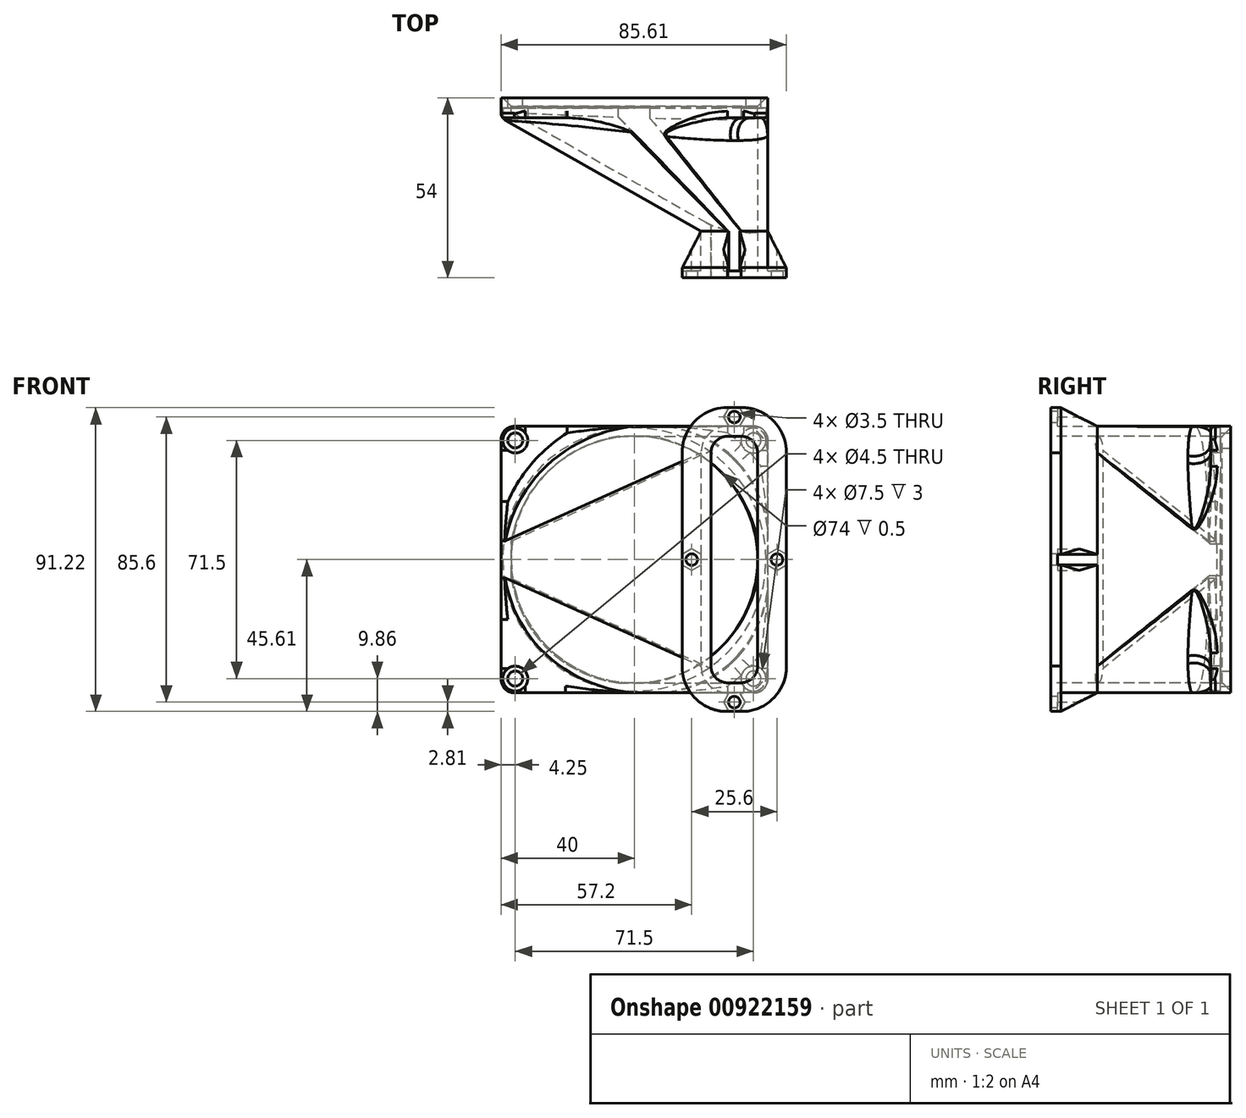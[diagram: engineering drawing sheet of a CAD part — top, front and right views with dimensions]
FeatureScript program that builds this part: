
annotation { "Feature Type Name" : "Feature", "Feature Type Description" : "" }
export const myFeature = defineFeature(function(context is Context, id is Id, definition is map)
    precondition{}
    {
        {
            var Q0;
            Q0=qCreatedBy(makeId("Front.planeOp"),FACE);
            var sketch = newSketch(context, id + "F0", { "sketchPlane" : qUnion([Q0])});
            skLineSegment(sketch, "E0.bottom", {"start": v(40, -40) * mm, "end": v(-40, -40) * mm});
            skLineSegment(sketch, "E0.top", {"start": v(40, 40) * mm, "end": v(-40, 40) * mm});
            skLineSegment(sketch, "E0.left", {"start": v(40, -40) * mm, "end": v(40, 40) * mm});
            skLineSegment(sketch, "E0.right", {"start": v(-40, -40) * mm, "end": v(-40, 40) * mm});
            skPoint(sketch, "E0.middle", {"position": v(0, 0) * mm});
            skCircle(sketch, "E1", {"center": v(0, 0) * mm, "radius": 37 * mm});
            skLineSegment(sketch, "E2.bottom", {"start": v(35.75, -35.75) * mm, "end": v(-35.75, -35.75) * mm, "construction": true});
            skLineSegment(sketch, "E2.top", {"start": v(35.75, 35.75) * mm, "end": v(-35.75, 35.75) * mm, "construction": true});
            skLineSegment(sketch, "E2.left", {"start": v(35.75, -35.75) * mm, "end": v(35.75, 35.75) * mm, "construction": true});
            skLineSegment(sketch, "E2.right", {"start": v(-35.75, -35.75) * mm, "end": v(-35.75, 35.75) * mm, "construction": true});
            skCircle(sketch, "E3", {"center": v(-35.75, 35.75) * mm, "radius": 2.25 * mm});
            skCircle(sketch, "E4", {"center": v(35.75, 35.75) * mm, "radius": 2.25 * mm});
            skCircle(sketch, "E5", {"center": v(-35.75, -35.75) * mm, "radius": 2.25 * mm});
            skCircle(sketch, "E6", {"center": v(35.75, -35.75) * mm, "radius": 2.25 * mm});
            skSolve(sketch);
        }
        {
            var Q0;
            Q0 = qSketchRegion(id + "F0", true);
            extrude(context, id + "F1", {"entities" : qUnion([Q0]), "depth" : 3 * mm, "offsetDistance" : 25 * mm});
        }
        {
            var Q0;
            Q0=makeQuery(id+"F1.opExtrude","CAP_FACE",FACE,{"disambiguationData":[OSD([sQuery(id+"F0.wireOp",EDGE,"E0.bottom"),sQuery(id+"F0.wireOp",EDGE,"E0.top"),sQuery(id+"F0.wireOp",EDGE,"E0.left"),sQuery(id+"F0.wireOp",EDGE,"E0.right"),sQuery(id+"F0.wireOp",EDGE,"E1"),sQuery(id+"F0.wireOp",EDGE,"E3"),sQuery(id+"F0.wireOp",EDGE,"E4"),sQuery(id+"F0.wireOp",EDGE,"E5"),sQuery(id+"F0.wireOp",EDGE,"E6")])],"isStart":false});
            var sketch = newSketch(context, id + "F2", { "sketchPlane" : qUnion([Q0])});
            skLineSegment(sketch, "E7", {"start": v(-5, 40) * mm, "end": v(0, 40) * mm});
            skLineSegment(sketch, "E8", {"start": v(40, -5) * mm, "end": v(40, 0) * mm});
            skLineSegment(sketch, "E9", {"start": v(0, -40) * mm, "end": v(-5, -40) * mm});
            skLineSegment(sketch, "E10", {"start": v(-40, 0) * mm, "end": v(-40, -5) * mm});
            skLineSegment(sketch, "E11", {"start": v(-40, 0) * mm, "end": v(-40, 5) * mm});
            skLineSegment(sketch, "E12", {"start": v(0, 40) * mm, "end": v(5, 40) * mm});
            skLineSegment(sketch, "E13", {"start": v(0, -40) * mm, "end": v(5, -40) * mm});
            skLineSegment(sketch, "E14", {"start": v(40, 0) * mm, "end": v(40, 5) * mm});
            skArc(sketch, "E15", {"start": v(-40, -5) * mm, "mid": v(-28.53, -28.53) * mm, "end": v(-5, -40) * mm});
            skArc(sketch, "E16", {"start": v(-5, 40) * mm, "mid": v(-28.28, 28.28) * mm, "end": v(-40, 5) * mm});
            skArc(sketch, "E17", {"start": v(40, 5) * mm, "mid": v(28.28, 28.28) * mm, "end": v(5, 40) * mm});
            skArc(sketch, "E18", {"start": v(5, -40) * mm, "mid": v(28.28, -28.28) * mm, "end": v(40, -5) * mm});
            skSolve(sketch);
        }
        {
            var Q0;
            Q0 = qSketchRegion(id + "F2", true);
            extrude(context, id + "F3", {"entities" : qUnion([Q0]), "operationType" : NewBodyOperationType.ADD, "depth" : 3 * mm, "offsetDistance" : 25 * mm});
        }
        {
            var Q0;
            Q0=makeQuery(id+"F1.opExtrude","CAP_FACE",FACE,{"disambiguationData":[OSD([sQuery(id+"F0.wireOp",EDGE,"E0.bottom"),sQuery(id+"F0.wireOp",EDGE,"E0.top"),sQuery(id+"F0.wireOp",EDGE,"E0.left"),sQuery(id+"F0.wireOp",EDGE,"E0.right"),sQuery(id+"F0.wireOp",EDGE,"E1"),sQuery(id+"F0.wireOp",EDGE,"E3"),sQuery(id+"F0.wireOp",EDGE,"E4"),sQuery(id+"F0.wireOp",EDGE,"E5"),sQuery(id+"F0.wireOp",EDGE,"E6")])],"isStart":true});
            cPlane(context, id + "F4", {"entities" : qUnion([Q0]), "cplaneType" : CPlaneType.OFFSET, "offset" : 40 * mm, "oppositeDirection" : true, "width" : 150 * mm, "height" : 150 * mm});
        }
        {
            var Q0;
            Q0=qCreatedBy(id+"F4.planeOp",FACE);
            var sketch = newSketch(context, id + "F5", { "sketchPlane" : qUnion([Q0])});
            skLineSegment(sketch, "E19.bottom", {"start": v(-28, 40) * mm, "end": v(-32, 40) * mm});
            skLineSegment(sketch, "E19.top", {"start": v(-28, -40) * mm, "end": v(-32, -40) * mm});
            skLineSegment(sketch, "E19.right", {"start": v(-40, 32) * mm, "end": v(-40, -32) * mm});
            skLineSegment(sketch, "E20", {"start": v(-20, 32) * mm, "end": v(-20, -32) * mm});
            skPoint(sketch, "E19.left.start.orphan", {"position": v(0, 40) * mm});
            skPoint(sketch, "E21.visualSharp", {"position": v(-40, -40) * mm});
            skArc(sketch, "E21.filletArc", {"start": v(-40, -32) * mm, "mid": v(-37.66, -37.66) * mm, "end": v(-32, -40) * mm});
            skPoint(sketch, "E22.visualSharp", {"position": v(-20, -40) * mm});
            skArc(sketch, "E22.filletArc", {"start": v(-28, -40) * mm, "mid": v(-22.34, -37.66) * mm, "end": v(-20, -32) * mm});
            skPoint(sketch, "E23.visualSharp", {"position": v(-20, 40) * mm});
            skArc(sketch, "E23.filletArc", {"start": v(-20, 32) * mm, "mid": v(-22.34, 37.66) * mm, "end": v(-28, 40) * mm});
            skPoint(sketch, "E24.visualSharp", {"position": v(-40, 40) * mm});
            skArc(sketch, "E24.filletArc", {"start": v(-32, 40) * mm, "mid": v(-37.66, 37.66) * mm, "end": v(-40, 32) * mm});
            skSolve(sketch);
        }
        {
            var Q1;
            Q1=makeQuery(id+"F3.opExtrude","CAP_FACE",FACE,{"disambiguationData":[OSD([sQuery(id+"F2.wireOp",EDGE,"E7"),sQuery(id+"F2.wireOp",EDGE,"E8"),sQuery(id+"F2.wireOp",EDGE,"E9"),sQuery(id+"F2.wireOp",EDGE,"E10"),sQuery(id+"F2.wireOp",EDGE,"E11"),sQuery(id+"F2.wireOp",EDGE,"E12"),sQuery(id+"F2.wireOp",EDGE,"E13"),sQuery(id+"F2.wireOp",EDGE,"E14"),sQuery(id+"F2.wireOp",EDGE,"E15"),sQuery(id+"F2.wireOp",EDGE,"E16"),sQuery(id+"F2.wireOp",EDGE,"E17"),sQuery(id+"F2.wireOp",EDGE,"E18")])],"isStart":false});
            var Q2;
            Q2=makeQuery(id+"F5.imprint","IMPRINT",FACE,{"disambiguationData":[TD([[makeQuery(id+"F5.imprint","IMPRINT",EDGE,{"derivedFrom":sQuery(id+"F5.wireOp",EDGE,"E19.bottom")}),1.0]])]});
            loft(context, id + "F6", {"operationType" : NewBodyOperationType.ADD, "sheetProfilesArray" : [{ "sheetProfileEntities" : qUnion([Q1]) }, { "sheetProfileEntities" : qUnion([Q2]) }]});
        }
        {
            var Q0;
            Q0=makeQuery(id+"F6.opLoft","CAP_FACE",FACE,{"disambiguationData":[OSD([makeQuery(id+"F5.imprint","IMPRINT",FACE,{"disambiguationData":[TD([[makeQuery(id+"F5.imprint","IMPRINT",EDGE,{"derivedFrom":sQuery(id+"F5.wireOp",EDGE,"E19.bottom")}),1.0]])]})])],"isStart":true});
            extrude(context, id + "F7", {"entities" : qUnion([Q0]), "operationType" : NewBodyOperationType.ADD, "depth" : 14 * mm, "offsetDistance" : 25 * mm});
        }
        {
            var Q0;
            Q0=makeQuery(id+"F7.opExtrude","CAP_FACE",FACE,{"disambiguationData":[OSD([makeQuery(id+"F5.imprint","IMPRINT",FACE,{"disambiguationData":[TD([[makeQuery(id+"F5.imprint","IMPRINT",EDGE,{"derivedFrom":sQuery(id+"F5.wireOp",EDGE,"E19.bottom")}),1.0]])]})])],"isStart":false});
            var Q1;
            Q1=makeQuery(id+"F3.opExtrude","CAP_FACE",FACE,{"disambiguationData":[OSD([sQuery(id+"F2.wireOp",EDGE,"E7"),sQuery(id+"F2.wireOp",EDGE,"E8"),sQuery(id+"F2.wireOp",EDGE,"E9"),sQuery(id+"F2.wireOp",EDGE,"E10"),sQuery(id+"F2.wireOp",EDGE,"E11"),sQuery(id+"F2.wireOp",EDGE,"E12"),sQuery(id+"F2.wireOp",EDGE,"E13"),sQuery(id+"F2.wireOp",EDGE,"E14"),sQuery(id+"F2.wireOp",EDGE,"E15"),sQuery(id+"F2.wireOp",EDGE,"E16"),sQuery(id+"F2.wireOp",EDGE,"E17"),sQuery(id+"F2.wireOp",EDGE,"E18")])],"isStart":true});
            shell(context, id + "F8", {"entities" : qUnion([Q0, Q1]), "thickness" : 3 * mm});
        }
        {
            var Q0;
            {var subQ0=sQuery(id+"F0.wireOp",EDGE,"E5");var subQ1=sQuery(id+"F0.wireOp",EDGE,"E0.right");var subQ2=sQuery(id+"F0.wireOp",EDGE,"E0.bottom");Q0=makeQuery(id+"F3.boolean.opBoolean","SPLIT",FACE,{"disambiguationData":[TD([makeQuery(id+"F1.opExtrude","SWEPT_FACE",FACE,{"disambiguationData":[OSD([subQ0])]})])],"derivedFrom":makeQuery(id+"F1.opExtrude","CAP_FACE",FACE,{"disambiguationData":[OSD([subQ2,sQuery(id+"F0.wireOp",EDGE,"E0.top"),sQuery(id+"F0.wireOp",EDGE,"E0.left"),subQ1,sQuery(id+"F0.wireOp",EDGE,"E1"),sQuery(id+"F0.wireOp",EDGE,"E3"),sQuery(id+"F0.wireOp",EDGE,"E4"),subQ0,sQuery(id+"F0.wireOp",EDGE,"E6")])],"isStart":false})});}
            var Q1;
            {var subQ0=sQuery(id+"F0.wireOp",EDGE,"E0.left");var subQ1=sQuery(id+"F0.wireOp",EDGE,"E6");var subQ2=sQuery(id+"F0.wireOp",EDGE,"E0.bottom");Q1=makeQuery(id+"F3.boolean.opBoolean","SPLIT",FACE,{"disambiguationData":[TD([makeQuery(id+"F1.opExtrude","SWEPT_FACE",FACE,{"disambiguationData":[OSD([subQ1])]})])],"derivedFrom":makeQuery(id+"F1.opExtrude","CAP_FACE",FACE,{"disambiguationData":[OSD([subQ2,sQuery(id+"F0.wireOp",EDGE,"E0.top"),subQ0,sQuery(id+"F0.wireOp",EDGE,"E0.right"),sQuery(id+"F0.wireOp",EDGE,"E1"),sQuery(id+"F0.wireOp",EDGE,"E3"),sQuery(id+"F0.wireOp",EDGE,"E4"),sQuery(id+"F0.wireOp",EDGE,"E5"),subQ1])],"isStart":false})});}
            var Q2;
            {var subQ0=sQuery(id+"F0.wireOp",EDGE,"E3");var subQ1=sQuery(id+"F0.wireOp",EDGE,"E0.right");var subQ2=sQuery(id+"F0.wireOp",EDGE,"E0.top");Q2=makeQuery(id+"F3.boolean.opBoolean","SPLIT",FACE,{"disambiguationData":[TD([makeQuery(id+"F1.opExtrude","SWEPT_FACE",FACE,{"disambiguationData":[OSD([subQ0])]})])],"derivedFrom":makeQuery(id+"F1.opExtrude","CAP_FACE",FACE,{"disambiguationData":[OSD([sQuery(id+"F0.wireOp",EDGE,"E0.bottom"),subQ2,sQuery(id+"F0.wireOp",EDGE,"E0.left"),subQ1,sQuery(id+"F0.wireOp",EDGE,"E1"),subQ0,sQuery(id+"F0.wireOp",EDGE,"E4"),sQuery(id+"F0.wireOp",EDGE,"E5"),sQuery(id+"F0.wireOp",EDGE,"E6")])],"isStart":false})});}
            var Q3;
            {var subQ0=sQuery(id+"F0.wireOp",EDGE,"E4");var subQ1=sQuery(id+"F0.wireOp",EDGE,"E0.left");var subQ2=sQuery(id+"F0.wireOp",EDGE,"E0.top");Q3=makeQuery(id+"F3.boolean.opBoolean","SPLIT",FACE,{"disambiguationData":[TD([makeQuery(id+"F1.opExtrude","SWEPT_FACE",FACE,{"disambiguationData":[OSD([subQ0])]})])],"derivedFrom":makeQuery(id+"F1.opExtrude","CAP_FACE",FACE,{"disambiguationData":[OSD([sQuery(id+"F0.wireOp",EDGE,"E0.bottom"),subQ2,subQ1,sQuery(id+"F0.wireOp",EDGE,"E0.right"),sQuery(id+"F0.wireOp",EDGE,"E1"),sQuery(id+"F0.wireOp",EDGE,"E3"),subQ0,sQuery(id+"F0.wireOp",EDGE,"E5"),sQuery(id+"F0.wireOp",EDGE,"E6")])],"isStart":false})});}
            var Q4;
            {var subQ0=sQuery(id+"F2.wireOp",EDGE,"E15");var subQ1=sQuery(id+"F2.wireOp",EDGE,"E9");var subQ2=sQuery(id+"F0.wireOp",EDGE,"E0.bottom");Q4=makeQuery(id+"F6.boolean.opBoolean","MERGE",VERTEX,{"derivedFrom":[makeQuery(id+"F3.opExtrude","CAP_VERTEX",VERTEX,{"disambiguationData":[OSD([subQ2,subQ1,subQ0])],"isStart":false}),makeQuery(id+"F6.opLoft","MID_CAP_VERTEX",VERTEX,{"disambiguationData":[OSD([subQ2,subQ1,subQ0])],"capPos":0.0})]});}
            extrude(context, id + "F9", {"entities" : qUnion([Q0, Q1, Q2, Q3]), "operationType" : NewBodyOperationType.ADD, "endBound" : BoundingType.UP_TO_VERTEX, "depth" : 25 * mm, "endBoundEntityVertex" : qUnion([Q4]), "offsetDistance" : 25 * mm});
        }
        {
            var Q0;
            {var subQ0=sQuery(id+"F0.wireOp",EDGE,"E5");var subQ1=sQuery(id+"F0.wireOp",EDGE,"E0.right");var subQ2=sQuery(id+"F0.wireOp",EDGE,"E0.bottom");var subQ3=sQuery(id+"F0.wireOp",EDGE,"E6");var subQ4=sQuery(id+"F0.wireOp",EDGE,"E4");var subQ5=sQuery(id+"F0.wireOp",EDGE,"E3");var subQ6=sQuery(id+"F0.wireOp",EDGE,"E1");var subQ7=sQuery(id+"F0.wireOp",EDGE,"E0.left");var subQ8=sQuery(id+"F0.wireOp",EDGE,"E0.top");Q0=makeQuery(id+"F9.opExtrude","CAP_FACE",FACE,{"disambiguationData":[OSD([subQ2,subQ8,subQ7,subQ1,subQ6,subQ5,subQ4,subQ0,subQ3]),TDD([makeQuery(id+"F3.boolean.opBoolean","SPLIT",FACE,{"disambiguationData":[TD([makeQuery(id+"F1.opExtrude","SWEPT_FACE",FACE,{"disambiguationData":[OSD([subQ0])]})])],"derivedFrom":makeQuery(id+"F1.opExtrude","CAP_FACE",FACE,{"disambiguationData":[OSD([subQ2,subQ8,subQ7,subQ1,subQ6,subQ5,subQ4,subQ0,subQ3])],"isStart":false})})])],"isStart":false});}
            var sketch = newSketch(context, id + "F10", { "sketchPlane" : qUnion([Q0])});
            skCircle(sketch, "E25", {"center": v(-35.75, -35.75) * mm, "radius": 3.75 * mm});
            skCircle(sketch, "E26", {"center": v(35.75, -35.75) * mm, "radius": 3.75 * mm});
            skCircle(sketch, "E27", {"center": v(35.75, 35.75) * mm, "radius": 3.75 * mm});
            skCircle(sketch, "E28", {"center": v(-35.75, 35.75) * mm, "radius": 3.75 * mm});
            skSolve(sketch);
        }
        {
            var Q0;
            Q0 = qSketchRegion(id + "F10", true);
            extrude(context, id + "F11", {"entities" : qUnion([Q0]), "operationType" : NewBodyOperationType.REMOVE, "oppositeDirection" : true, "depth" : 3 * mm, "offsetDistance" : 25 * mm});
        }
        {
            var Q0;
            {var subQ0=sQuery(id+"F0.wireOp",EDGE,"E0.left");var subQ1=sQuery(id+"F0.wireOp",EDGE,"E0.bottom");Q0=makeQuery(id+"F9.boolean.opBoolean","MERGE",EDGE,{"derivedFrom":[makeQuery(id+"F1.opExtrude","SWEPT_EDGE",EDGE,{"disambiguationData":[OSD([subQ1,subQ0])]}),makeQuery(id+"F9.opExtrude","SWEPT_EDGE",EDGE,{"disambiguationData":[OSD([subQ1,subQ0])]})]});}
            var Q1;
            {var subQ0=sQuery(id+"F0.wireOp",EDGE,"E0.left");var subQ1=sQuery(id+"F0.wireOp",EDGE,"E0.top");Q1=makeQuery(id+"F9.boolean.opBoolean","MERGE",EDGE,{"derivedFrom":[makeQuery(id+"F1.opExtrude","SWEPT_EDGE",EDGE,{"disambiguationData":[OSD([subQ1,subQ0])]}),makeQuery(id+"F9.opExtrude","SWEPT_EDGE",EDGE,{"disambiguationData":[OSD([subQ1,subQ0])]})]});}
            var Q2;
            {var subQ0=sQuery(id+"F0.wireOp",EDGE,"E0.right");var subQ1=sQuery(id+"F0.wireOp",EDGE,"E0.bottom");Q2=makeQuery(id+"F9.boolean.opBoolean","MERGE",EDGE,{"derivedFrom":[makeQuery(id+"F1.opExtrude","SWEPT_EDGE",EDGE,{"disambiguationData":[OSD([subQ1,subQ0])]}),makeQuery(id+"F9.opExtrude","SWEPT_EDGE",EDGE,{"disambiguationData":[OSD([subQ1,subQ0])]})]});}
            var Q3;
            {var subQ0=sQuery(id+"F0.wireOp",EDGE,"E0.right");var subQ1=sQuery(id+"F0.wireOp",EDGE,"E0.top");Q3=makeQuery(id+"F9.boolean.opBoolean","MERGE",EDGE,{"derivedFrom":[makeQuery(id+"F1.opExtrude","SWEPT_EDGE",EDGE,{"disambiguationData":[OSD([subQ1,subQ0])]}),makeQuery(id+"F9.opExtrude","SWEPT_EDGE",EDGE,{"disambiguationData":[OSD([subQ1,subQ0])]})]});}
            fillet(context, id + "F12", {"entities" : qUnion([Q0, Q1, Q2, Q3]), "radius" : 4 * mm, "tangentPropagation" : true, "allowEdgeOverflow" : false});
        }
        {
            var Q0;
            {var subQ0=sQuery(id+"F2.wireOp",EDGE,"E18");Q0=makeQuery(id+"F9.boolean.opBoolean","MERGE",EDGE,{"derivedFrom":[makeQuery(id+"F6.boolean.opBoolean","MERGE",EDGE,{"derivedFrom":[makeQuery(id+"F3.opExtrude","CAP_EDGE",EDGE,{"disambiguationData":[OSD([subQ0])],"isStart":false}),makeQuery(id+"F6.opLoft","MID_CAP_EDGE",EDGE,{"disambiguationData":[OSD([sQuery(id+"F0.wireOp",EDGE,"E0.bottom"),sQuery(id+"F0.wireOp",EDGE,"E0.left"),sQuery(id+"F2.wireOp",EDGE,"E8"),sQuery(id+"F2.wireOp",EDGE,"E13"),subQ0])],"capPos":0.0})]}),makeQuery(id+"F9.opExtrude","CAP_EDGE",EDGE,{"disambiguationData":[OSD([subQ0])],"isStart":false})]});}
            var Q1;
            {var subQ0=sQuery(id+"F2.wireOp",EDGE,"E15");Q1=makeQuery(id+"F9.boolean.opBoolean","MERGE",EDGE,{"derivedFrom":[makeQuery(id+"F6.boolean.opBoolean","MERGE",EDGE,{"derivedFrom":[makeQuery(id+"F3.opExtrude","CAP_EDGE",EDGE,{"disambiguationData":[OSD([subQ0])],"isStart":false}),makeQuery(id+"F6.opLoft","MID_CAP_EDGE",EDGE,{"disambiguationData":[OSD([sQuery(id+"F0.wireOp",EDGE,"E0.bottom"),sQuery(id+"F0.wireOp",EDGE,"E0.right"),sQuery(id+"F2.wireOp",EDGE,"E9"),sQuery(id+"F2.wireOp",EDGE,"E10"),subQ0])],"capPos":0.0})]}),makeQuery(id+"F9.opExtrude","CAP_EDGE",EDGE,{"disambiguationData":[OSD([subQ0])],"isStart":false})]});}
            var Q2;
            {var subQ0=sQuery(id+"F2.wireOp",EDGE,"E17");Q2=makeQuery(id+"F9.boolean.opBoolean","MERGE",EDGE,{"derivedFrom":[makeQuery(id+"F6.boolean.opBoolean","MERGE",EDGE,{"derivedFrom":[makeQuery(id+"F3.opExtrude","CAP_EDGE",EDGE,{"disambiguationData":[OSD([subQ0])],"isStart":false}),makeQuery(id+"F6.opLoft","MID_CAP_EDGE",EDGE,{"disambiguationData":[OSD([sQuery(id+"F0.wireOp",EDGE,"E0.top"),sQuery(id+"F0.wireOp",EDGE,"E0.left"),sQuery(id+"F2.wireOp",EDGE,"E12"),sQuery(id+"F2.wireOp",EDGE,"E14"),subQ0])],"capPos":0.0})]}),makeQuery(id+"F9.opExtrude","CAP_EDGE",EDGE,{"disambiguationData":[OSD([subQ0])],"isStart":false})]});}
            var Q3;
            {var subQ0=sQuery(id+"F2.wireOp",EDGE,"E16");Q3=makeQuery(id+"F9.boolean.opBoolean","MERGE",EDGE,{"derivedFrom":[makeQuery(id+"F6.boolean.opBoolean","MERGE",EDGE,{"derivedFrom":[makeQuery(id+"F3.opExtrude","CAP_EDGE",EDGE,{"disambiguationData":[OSD([subQ0])],"isStart":false}),makeQuery(id+"F6.opLoft","MID_CAP_EDGE",EDGE,{"disambiguationData":[OSD([sQuery(id+"F0.wireOp",EDGE,"E0.top"),sQuery(id+"F0.wireOp",EDGE,"E0.right"),sQuery(id+"F2.wireOp",EDGE,"E7"),sQuery(id+"F2.wireOp",EDGE,"E11"),subQ0])],"capPos":0.0})]}),makeQuery(id+"F9.opExtrude","CAP_EDGE",EDGE,{"disambiguationData":[OSD([subQ0])],"isStart":false})]});}
            fillet(context, id + "F13", {"entities" : qUnion([Q0, Q1, Q2, Q3]), "radius" : 5 * mm, "tangentPropagation" : true, "allowEdgeOverflow" : false});
        }
        {
            var Q0;
            {var subQ0=sQuery(id+"F0.wireOp",EDGE,"E0.right");var subQ1=sQuery(id+"F0.wireOp",EDGE,"E0.top");Q0=makeQuery(id+"F9.opExtrude","CAP_EDGE",EDGE,{"disambiguationData":[OSD([subQ1]),TDD([makeQuery(id+"F3.boolean.opBoolean","SPLIT",EDGE,{"disambiguationData":[TD([makeQuery(id+"F1.opExtrude","SWEPT_FACE",FACE,{"disambiguationData":[OSD([subQ0])]})])],"derivedFrom":makeQuery(id+"F1.opExtrude","CAP_EDGE",EDGE,{"disambiguationData":[OSD([subQ1])],"isStart":false})})])],"isStart":false});}
            var Q1;
            {var subQ0=sQuery(id+"F0.wireOp",EDGE,"E0.right");var subQ1=sQuery(id+"F0.wireOp",EDGE,"E0.bottom");Q1=makeQuery(id+"F9.opExtrude","CAP_EDGE",EDGE,{"disambiguationData":[OSD([subQ0]),TDD([makeQuery(id+"F3.boolean.opBoolean","SPLIT",EDGE,{"disambiguationData":[TD([makeQuery(id+"F1.opExtrude","SWEPT_FACE",FACE,{"disambiguationData":[OSD([subQ1])]})])],"derivedFrom":makeQuery(id+"F1.opExtrude","CAP_EDGE",EDGE,{"disambiguationData":[OSD([subQ0])],"isStart":false})})])],"isStart":false});}
            var Q2;
            {var subQ0=sQuery(id+"F0.wireOp",EDGE,"E0.left");var subQ1=sQuery(id+"F0.wireOp",EDGE,"E0.bottom");Q2=makeQuery(id+"F9.opExtrude","CAP_EDGE",EDGE,{"disambiguationData":[OSD([subQ1]),TDD([makeQuery(id+"F3.boolean.opBoolean","SPLIT",EDGE,{"disambiguationData":[TD([makeQuery(id+"F1.opExtrude","SWEPT_FACE",FACE,{"disambiguationData":[OSD([subQ0])]})])],"derivedFrom":makeQuery(id+"F1.opExtrude","CAP_EDGE",EDGE,{"disambiguationData":[OSD([subQ1])],"isStart":false})})])],"isStart":false});}
            var Q3;
            {var subQ0=sQuery(id+"F0.wireOp",EDGE,"E0.left");var subQ1=sQuery(id+"F0.wireOp",EDGE,"E0.top");Q3=makeQuery(id+"F9.opExtrude","CAP_EDGE",EDGE,{"disambiguationData":[OSD([subQ0]),TDD([makeQuery(id+"F3.boolean.opBoolean","SPLIT",EDGE,{"disambiguationData":[TD([makeQuery(id+"F1.opExtrude","SWEPT_FACE",FACE,{"disambiguationData":[OSD([subQ1])]})])],"derivedFrom":makeQuery(id+"F1.opExtrude","CAP_EDGE",EDGE,{"disambiguationData":[OSD([subQ0])],"isStart":false})})])],"isStart":false});}
            fillet(context, id + "F14", {"entities" : qUnion([Q0, Q1, Q2, Q3]), "radius" : 2 * mm, "tangentPropagation" : true, "allowEdgeOverflow" : false});
        }
        {
            var Q0;
            Q0=makeQuery(id+"F1.opExtrude","CAP_EDGE",EDGE,{"disambiguationData":[OSD([sQuery(id+"F0.wireOp",EDGE,"E1")])],"isStart":true});
            chamfer(context, id + "F15", {"entities" : qUnion([Q0]), "width" : 2.5 * mm, "tangentPropagation" : true});
        }
        {
            var Q0;
            Q0=makeQuery(id+"F7.opExtrude","CAP_FACE",FACE,{"disambiguationData":[OSD([makeQuery(id+"F5.imprint","IMPRINT",FACE,{"disambiguationData":[TD([[makeQuery(id+"F5.imprint","IMPRINT",EDGE,{"derivedFrom":sQuery(id+"F5.wireOp",EDGE,"E19.bottom")}),1.0]])]})])],"isStart":false});
            var sketch = newSketch(context, id + "F16", { "sketchPlane" : qUnion([Q0])});
            skFitSpline(sketch, "E29.0", {"points": [v(28, 45.6) * mm, v(27.11, 45.6) * mm, v(25.33, 45.42) * mm, v(22.76, 44.65) * mm, v(20.4, 43.38) * mm, v(18.32, 41.68) * mm, v(16.62, 39.6) * mm, v(15.35, 37.24) * mm, v(14.58, 34.67) * mm, v(14.4, 32.9) * mm, v(14.4, 32) * mm]});
            skLineSegment(sketch, "E29.1", {"start": v(32, 45.6) * mm, "end": v(28, 45.6) * mm});
            skLineSegment(sketch, "E29.2", {"start": v(14.4, 32) * mm, "end": v(14.4, -32) * mm});
            skFitSpline(sketch, "E29.3", {"points": [v(45.6, 32) * mm, v(45.6, 32.89) * mm, v(45.42, 34.67) * mm, v(44.65, 37.24) * mm, v(43.38, 39.6) * mm, v(41.68, 41.68) * mm, v(39.6, 43.38) * mm, v(37.24, 44.65) * mm, v(34.67, 45.42) * mm, v(32.9, 45.6) * mm, v(32, 45.6) * mm]});
            skFitSpline(sketch, "E29.4", {"points": [v(14.4, -32) * mm, v(14.4, -32.89) * mm, v(14.58, -34.67) * mm, v(15.35, -37.24) * mm, v(16.62, -39.6) * mm, v(18.32, -41.68) * mm, v(20.4, -43.38) * mm, v(22.76, -44.65) * mm, v(25.33, -45.42) * mm, v(27.1, -45.6) * mm, v(28, -45.6) * mm]});
            skLineSegment(sketch, "E29.5", {"start": v(28, -45.6) * mm, "end": v(32, -45.6) * mm});
            skFitSpline(sketch, "E29.6", {"points": [v(32, -45.6) * mm, v(32.89, -45.6) * mm, v(34.67, -45.42) * mm, v(37.24, -44.65) * mm, v(39.6, -43.38) * mm, v(41.68, -41.68) * mm, v(43.38, -39.6) * mm, v(44.65, -37.24) * mm, v(45.42, -34.67) * mm, v(45.6, -32.9) * mm, v(45.6, -32) * mm]});
            skLineSegment(sketch, "E29.7", {"start": v(45.6, -32) * mm, "end": v(45.6, 32) * mm});
            skLineSegment(sketch, "E30.0", {"start": v(17.2, 32) * mm, "end": v(17.2, -32) * mm, "construction": true});
            skFitSpline(sketch, "E30.1", {"points": [v(28, 42.8) * mm, v(27.3, 42.8) * mm, v(25.88, 42.66) * mm, v(23.16, 41.84) * mm, v(20.16, 39.84) * mm, v(18.16, 36.84) * mm, v(17.34, 34.12) * mm, v(17.2, 32.7) * mm, v(17.2, 32) * mm], "construction": true});
            skFitSpline(sketch, "E30.2", {"points": [v(17.2, -32) * mm, v(17.2, -32.7) * mm, v(17.34, -34.12) * mm, v(18.16, -36.84) * mm, v(20.16, -39.84) * mm, v(23.16, -41.84) * mm, v(25.88, -42.66) * mm, v(27.3, -42.8) * mm, v(28, -42.8) * mm], "construction": true});
            skLineSegment(sketch, "E30.3", {"start": v(32, 42.8) * mm, "end": v(28, 42.8) * mm, "construction": true});
            skLineSegment(sketch, "E30.4", {"start": v(28, -42.8) * mm, "end": v(32, -42.8) * mm, "construction": true});
            skFitSpline(sketch, "E30.5", {"points": [v(32, -42.8) * mm, v(32.7, -42.8) * mm, v(34.12, -42.66) * mm, v(36.84, -41.84) * mm, v(39.84, -39.84) * mm, v(41.84, -36.84) * mm, v(42.66, -34.12) * mm, v(42.8, -32.7) * mm, v(42.8, -32) * mm], "construction": true});
            skLineSegment(sketch, "E30.6", {"start": v(42.8, -32) * mm, "end": v(42.8, 32) * mm, "construction": true});
            skFitSpline(sketch, "E30.7", {"points": [v(42.8, 32) * mm, v(42.8, 32.7) * mm, v(42.66, 34.12) * mm, v(41.84, 36.84) * mm, v(39.84, 39.84) * mm, v(36.84, 41.84) * mm, v(34.12, 42.66) * mm, v(32.7, 42.8) * mm, v(32, 42.8) * mm], "construction": true});
            skCircle(sketch, "E31", {"center": v(30, -42.8) * mm, "radius": 1.75 * mm});
            skCircle(sketch, "E32", {"center": v(30, 42.8) * mm, "radius": 1.75 * mm});
            skCircle(sketch, "E33", {"center": v(42.8, 0) * mm, "radius": 1.75 * mm});
            skCircle(sketch, "E34", {"center": v(17.2, 0) * mm, "radius": 1.75 * mm});
            skSolve(sketch);
        }
        {
            var Q0;
            Q0=makeQuery(id+"F16.imprint","IMPRINT",FACE,{"disambiguationData":[TD([[makeQuery(id+"F16.imprint","IMPRINT",EDGE,{"derivedFrom":sQuery(id+"F16.wireOp",EDGE,"E29.0")}),1.0]])]});
            var Q1;
            {var subQ0=sQuery(id+"F5.wireOp",EDGE,"E23.filletArc");var subQ2=sQuery(id+"F5.wireOp",EDGE,"E19.bottom");var subQ4=sQuery(id+"F5.wireOp",EDGE,"E24.filletArc");Q1=makeQuery(id+"F16.imprint","IMPRINT",FACE,{"disambiguationData":[TD([[makeQuery(id+"F16.imprint","IMPRINT",EDGE,{"derivedFrom":makeQuery(id+"F7.opExtrude","CAP_EDGE",EDGE,{"disambiguationData":[OSD([subQ2,subQ0,subQ4])],"isStart":false})}),1.0]])]});}
            extrude(context, id + "F17", {"entities" : qUnion([Q0, Q1]), "operationType" : NewBodyOperationType.ADD, "oppositeDirection" : true, "depth" : 3 * mm, "offsetDistance" : 25 * mm});
        }
        {
            var Q0;
            Q0=makeQuery(id+"F17.opExtrude","CAP_FACE",FACE,{"disambiguationData":[OSD([sQuery(id+"F5.wireOp",EDGE,"E19.bottom"),sQuery(id+"F5.wireOp",EDGE,"E19.top"),sQuery(id+"F5.wireOp",EDGE,"E19.right"),sQuery(id+"F5.wireOp",EDGE,"E20"),sQuery(id+"F5.wireOp",EDGE,"E21.filletArc"),sQuery(id+"F5.wireOp",EDGE,"E22.filletArc"),sQuery(id+"F5.wireOp",EDGE,"E23.filletArc"),sQuery(id+"F5.wireOp",EDGE,"E24.filletArc"),sQuery(id+"F16.wireOp",EDGE,"E29.0"),sQuery(id+"F16.wireOp",EDGE,"E29.1"),sQuery(id+"F16.wireOp",EDGE,"E29.2"),sQuery(id+"F16.wireOp",EDGE,"E29.3"),sQuery(id+"F16.wireOp",EDGE,"E29.4"),sQuery(id+"F16.wireOp",EDGE,"E29.5"),sQuery(id+"F16.wireOp",EDGE,"E29.6"),sQuery(id+"F16.wireOp",EDGE,"E29.7"),sQuery(id+"F16.wireOp",EDGE,"E31"),sQuery(id+"F16.wireOp",EDGE,"E32"),sQuery(id+"F16.wireOp",EDGE,"E33"),sQuery(id+"F16.wireOp",EDGE,"E34")])],"isStart":false});
            var sketch = newSketch(context, id + "F18", { "sketchPlane" : qUnion([Q0])});
            skCircle(sketch, "E35.cCircle", {"center": v(-42.8, 0) * mm, "radius": 2.8 * mm, "construction": true});
            skLineSegment(sketch, "E35.0", {"start": v(-40, -1.62) * mm, "end": v(-42.8, -3.23) * mm});
            skLineSegment(sketch, "E35.1", {"start": v(-42.8, -3.23) * mm, "end": v(-45.6, -1.62) * mm});
            skLineSegment(sketch, "E35.2", {"start": v(-45.6, -1.62) * mm, "end": v(-45.6, 1.62) * mm});
            skLineSegment(sketch, "E35.3", {"start": v(-45.6, 1.62) * mm, "end": v(-42.8, 3.23) * mm});
            skLineSegment(sketch, "E35.4", {"start": v(-42.8, 3.23) * mm, "end": v(-40, 1.62) * mm});
            skLineSegment(sketch, "E35.5", {"start": v(-40, 1.62) * mm, "end": v(-40, -1.62) * mm});
            skPoint(sketch, "E35.0.midPoint", {"position": v(-41.4, -2.42) * mm});
            skCircle(sketch, "E36.cCircle", {"center": v(-30, 42.8) * mm, "radius": 2.8 * mm, "construction": true});
            skLineSegment(sketch, "E36.0", {"start": v(-26.77, 42.8) * mm, "end": v(-28.38, 40) * mm});
            skLineSegment(sketch, "E36.1", {"start": v(-28.38, 40) * mm, "end": v(-31.62, 40) * mm});
            skLineSegment(sketch, "E36.2", {"start": v(-31.62, 40) * mm, "end": v(-33.23, 42.8) * mm});
            skLineSegment(sketch, "E36.3", {"start": v(-33.23, 42.8) * mm, "end": v(-31.62, 45.6) * mm});
            skLineSegment(sketch, "E36.4", {"start": v(-31.62, 45.6) * mm, "end": v(-28.38, 45.6) * mm});
            skLineSegment(sketch, "E36.5", {"start": v(-28.38, 45.6) * mm, "end": v(-26.77, 42.8) * mm});
            skPoint(sketch, "E36.0.midPoint", {"position": v(-27.58, 41.4) * mm});
            skCircle(sketch, "E37.cCircle", {"center": v(-30, -42.8) * mm, "radius": 2.8 * mm, "construction": true});
            skLineSegment(sketch, "E37.0", {"start": v(-26.77, -42.8) * mm, "end": v(-28.38, -45.6) * mm});
            skLineSegment(sketch, "E37.1", {"start": v(-28.38, -45.6) * mm, "end": v(-31.62, -45.6) * mm});
            skLineSegment(sketch, "E37.2", {"start": v(-31.62, -45.6) * mm, "end": v(-33.23, -42.8) * mm});
            skLineSegment(sketch, "E37.3", {"start": v(-33.23, -42.8) * mm, "end": v(-31.62, -40) * mm});
            skLineSegment(sketch, "E37.4", {"start": v(-31.62, -40) * mm, "end": v(-28.38, -40) * mm});
            skLineSegment(sketch, "E37.5", {"start": v(-28.38, -40) * mm, "end": v(-26.77, -42.8) * mm});
            skPoint(sketch, "E37.0.midPoint", {"position": v(-27.58, -44.2) * mm});
            skCircle(sketch, "E38.cCircle", {"center": v(-17.2, 0) * mm, "radius": 2.8 * mm, "construction": true});
            skLineSegment(sketch, "E38.0", {"start": v(-14.4, -1.62) * mm, "end": v(-17.2, -3.23) * mm});
            skLineSegment(sketch, "E38.1", {"start": v(-17.2, -3.23) * mm, "end": v(-20, -1.62) * mm});
            skLineSegment(sketch, "E38.2", {"start": v(-20, -1.62) * mm, "end": v(-20, 1.62) * mm});
            skLineSegment(sketch, "E38.3", {"start": v(-20, 1.62) * mm, "end": v(-17.2, 3.23) * mm});
            skLineSegment(sketch, "E38.4", {"start": v(-17.2, 3.23) * mm, "end": v(-14.4, 1.62) * mm});
            skLineSegment(sketch, "E38.5", {"start": v(-14.4, 1.62) * mm, "end": v(-14.4, -1.62) * mm});
            skPoint(sketch, "E38.0.midPoint", {"position": v(-15.8, -2.42) * mm});
            skSolve(sketch);
        }
        {
            var Q0;
            Q0 = qSketchRegion(id + "F18", true);
            extrude(context, id + "F19", {"entities" : qUnion([Q0]), "operationType" : NewBodyOperationType.REMOVE, "oppositeDirection" : true, "depth" : 1 * mm, "offsetDistance" : 25 * mm});
        }
        {
            var Q0;
            {var subQ0=sQuery(id+"F5.wireOp",EDGE,"E22.filletArc");var subQ1=sQuery(id+"F5.wireOp",EDGE,"E20");var subQ2=sQuery(id+"F5.wireOp",EDGE,"E19.top");Q0=makeQuery(id+"F17.boolean.opBoolean","INTERSECT",EDGE,{"derivedFrom":[makeQuery(id+"F7.opExtrude","SWEPT_FACE",FACE,{"disambiguationData":[OSD([subQ2,subQ1,subQ0])]}),makeQuery(id+"F17.opExtrude","CAP_FACE",FACE,{"disambiguationData":[OSD([sQuery(id+"F5.wireOp",EDGE,"E19.bottom"),subQ2,sQuery(id+"F5.wireOp",EDGE,"E19.right"),subQ1,sQuery(id+"F5.wireOp",EDGE,"E21.filletArc"),subQ0,sQuery(id+"F5.wireOp",EDGE,"E23.filletArc"),sQuery(id+"F5.wireOp",EDGE,"E24.filletArc"),sQuery(id+"F16.wireOp",EDGE,"E29.0"),sQuery(id+"F16.wireOp",EDGE,"E29.1"),sQuery(id+"F16.wireOp",EDGE,"E29.2"),sQuery(id+"F16.wireOp",EDGE,"E29.3"),sQuery(id+"F16.wireOp",EDGE,"E29.4"),sQuery(id+"F16.wireOp",EDGE,"E29.5"),sQuery(id+"F16.wireOp",EDGE,"E29.6"),sQuery(id+"F16.wireOp",EDGE,"E29.7"),sQuery(id+"F16.wireOp",EDGE,"E31"),sQuery(id+"F16.wireOp",EDGE,"E32"),sQuery(id+"F16.wireOp",EDGE,"E33"),sQuery(id+"F16.wireOp",EDGE,"E34")])],"isStart":false})]});}
            var Q1;
            {var subQ0=sQuery(id+"F5.wireOp",EDGE,"E21.filletArc");var subQ1=sQuery(id+"F5.wireOp",EDGE,"E19.right");var subQ2=sQuery(id+"F5.wireOp",EDGE,"E19.top");Q1=makeQuery(id+"F17.boolean.opBoolean","INTERSECT",EDGE,{"derivedFrom":[makeQuery(id+"F7.opExtrude","SWEPT_FACE",FACE,{"disambiguationData":[OSD([subQ2,subQ1,subQ0])]}),makeQuery(id+"F17.opExtrude","CAP_FACE",FACE,{"disambiguationData":[OSD([sQuery(id+"F5.wireOp",EDGE,"E19.bottom"),subQ2,subQ1,sQuery(id+"F5.wireOp",EDGE,"E20"),subQ0,sQuery(id+"F5.wireOp",EDGE,"E22.filletArc"),sQuery(id+"F5.wireOp",EDGE,"E23.filletArc"),sQuery(id+"F5.wireOp",EDGE,"E24.filletArc"),sQuery(id+"F16.wireOp",EDGE,"E29.0"),sQuery(id+"F16.wireOp",EDGE,"E29.1"),sQuery(id+"F16.wireOp",EDGE,"E29.2"),sQuery(id+"F16.wireOp",EDGE,"E29.3"),sQuery(id+"F16.wireOp",EDGE,"E29.4"),sQuery(id+"F16.wireOp",EDGE,"E29.5"),sQuery(id+"F16.wireOp",EDGE,"E29.6"),sQuery(id+"F16.wireOp",EDGE,"E29.7"),sQuery(id+"F16.wireOp",EDGE,"E31"),sQuery(id+"F16.wireOp",EDGE,"E32"),sQuery(id+"F16.wireOp",EDGE,"E33"),sQuery(id+"F16.wireOp",EDGE,"E34")])],"isStart":false})]});}
            var Q2;
            {var subQ0=sQuery(id+"F5.wireOp",EDGE,"E24.filletArc");var subQ1=sQuery(id+"F5.wireOp",EDGE,"E19.right");var subQ2=sQuery(id+"F5.wireOp",EDGE,"E19.bottom");var subQ3=sQuery(id+"F5.wireOp",EDGE,"E21.filletArc");var subQ4=sQuery(id+"F2.wireOp",EDGE,"E18");var subQ5=sQuery(id+"F2.wireOp",EDGE,"E17");var subQ6=sQuery(id+"F2.wireOp",EDGE,"E14");var subQ7=sQuery(id+"F2.wireOp",EDGE,"E8");var subQ8=sQuery(id+"F0.wireOp",EDGE,"E0.left");var subQ9=makeQuery(id+"F6.opLoft","SWEPT_FACE",FACE,{"disambiguationData":[OSD([subQ8,subQ7,subQ6,subQ5,subQ4,subQ1,subQ3,subQ0])]});var subQ10=makeQuery(id+"F7.opExtrude","SWEPT_FACE",FACE,{"disambiguationData":[OSD([subQ1,subQ3,subQ0])]});var subQ11=makeQuery(id+"F1.opExtrude","SWEPT_FACE",FACE,{"disambiguationData":[OSD([subQ8])]});var subQ12=sQuery(id+"F0.wireOp",EDGE,"E0.top");var subQ13=sQuery(id+"F0.wireOp",EDGE,"E0.bottom");var subQ15=makeQuery(id+"F3.opExtrude","SWEPT_FACE",FACE,{"disambiguationData":[OSD([subQ7,subQ6])]});var subQ16=makeQuery(id+"F1.opExtrude","CAP_EDGE",EDGE,{"disambiguationData":[OSD([subQ8])],"isStart":false});var subQ17=makeQuery(id+"F9.opExtrude","SWEPT_FACE",FACE,{"disambiguationData":[OSD([subQ8]),TDD([makeQuery(id+"F3.boolean.opBoolean","SPLIT",EDGE,{"disambiguationData":[TD([makeQuery(id+"F1.opExtrude","SWEPT_FACE",FACE,{"disambiguationData":[OSD([subQ13])]})])],"derivedFrom":subQ16})])]});var subQ18=makeQuery(id+"F9.opExtrude","SWEPT_FACE",FACE,{"disambiguationData":[OSD([subQ8]),TDD([makeQuery(id+"F3.boolean.opBoolean","SPLIT",EDGE,{"disambiguationData":[TD([makeQuery(id+"F1.opExtrude","SWEPT_FACE",FACE,{"disambiguationData":[OSD([subQ12])]})])],"derivedFrom":subQ16})])]});var subQ19=makeQuery(id+"F17.opExtrude","CAP_FACE",FACE,{"disambiguationData":[OSD([subQ2,sQuery(id+"F5.wireOp",EDGE,"E19.top"),subQ1,sQuery(id+"F5.wireOp",EDGE,"E20"),subQ3,sQuery(id+"F5.wireOp",EDGE,"E22.filletArc"),sQuery(id+"F5.wireOp",EDGE,"E23.filletArc"),subQ0,sQuery(id+"F16.wireOp",EDGE,"E29.0"),sQuery(id+"F16.wireOp",EDGE,"E29.1"),sQuery(id+"F16.wireOp",EDGE,"E29.2"),sQuery(id+"F16.wireOp",EDGE,"E29.3"),sQuery(id+"F16.wireOp",EDGE,"E29.4"),sQuery(id+"F16.wireOp",EDGE,"E29.5"),sQuery(id+"F16.wireOp",EDGE,"E29.6"),sQuery(id+"F16.wireOp",EDGE,"E29.7"),sQuery(id+"F16.wireOp",EDGE,"E31"),sQuery(id+"F16.wireOp",EDGE,"E32"),sQuery(id+"F16.wireOp",EDGE,"E33"),sQuery(id+"F16.wireOp",EDGE,"E34")])],"isStart":false});Q2=makeQuery(id+"F19.boolean.opBoolean","SPLIT",EDGE,{"disambiguationData":[TD([makeQuery(id+"F19.opExtrude","SWEPT_FACE",FACE,{"disambiguationData":[OSD([sQuery(id+"F18.wireOp",EDGE,"E35.4")])]})])],"derivedFrom":makeQuery(id+"F17.boolean.opBoolean","INTERSECT",EDGE,{"derivedFrom":[makeQuery(id+"F9.boolean.opBoolean","MERGE",FACE,{"derivedFrom":[makeQuery(id+"F7.boolean.opBoolean","MERGE",FACE,{"derivedFrom":[makeQuery(id+"F6.boolean.opBoolean","MERGE",FACE,{"derivedFrom":[makeQuery(id+"F3.boolean.opBoolean","MERGE",FACE,{"derivedFrom":[subQ11,subQ15]}),subQ9]}),subQ10]}),subQ17,subQ18]}),subQ19]})});}
            var Q3;
            {var subQ0=sQuery(id+"F5.wireOp",EDGE,"E23.filletArc");var subQ1=sQuery(id+"F5.wireOp",EDGE,"E20");var subQ2=sQuery(id+"F5.wireOp",EDGE,"E19.bottom");Q3=makeQuery(id+"F17.boolean.opBoolean","INTERSECT",EDGE,{"derivedFrom":[makeQuery(id+"F7.opExtrude","SWEPT_FACE",FACE,{"disambiguationData":[OSD([subQ2,subQ1,subQ0])]}),makeQuery(id+"F17.opExtrude","CAP_FACE",FACE,{"disambiguationData":[OSD([subQ2,sQuery(id+"F5.wireOp",EDGE,"E19.top"),sQuery(id+"F5.wireOp",EDGE,"E19.right"),subQ1,sQuery(id+"F5.wireOp",EDGE,"E21.filletArc"),sQuery(id+"F5.wireOp",EDGE,"E22.filletArc"),subQ0,sQuery(id+"F5.wireOp",EDGE,"E24.filletArc"),sQuery(id+"F16.wireOp",EDGE,"E29.0"),sQuery(id+"F16.wireOp",EDGE,"E29.1"),sQuery(id+"F16.wireOp",EDGE,"E29.2"),sQuery(id+"F16.wireOp",EDGE,"E29.3"),sQuery(id+"F16.wireOp",EDGE,"E29.4"),sQuery(id+"F16.wireOp",EDGE,"E29.5"),sQuery(id+"F16.wireOp",EDGE,"E29.6"),sQuery(id+"F16.wireOp",EDGE,"E29.7"),sQuery(id+"F16.wireOp",EDGE,"E31"),sQuery(id+"F16.wireOp",EDGE,"E32"),sQuery(id+"F16.wireOp",EDGE,"E33"),sQuery(id+"F16.wireOp",EDGE,"E34")])],"isStart":false})]});}
            chamfer(context, id + "F20", {"entities" : qUnion([Q0, Q1, Q2, Q3]), "chamferType" : ChamferType.TWO_OFFSETS, "width1" : 5.6 * mm, "oppositeDirection" : false, "width2" : 11 * mm, "tangentPropagation" : true});
        }
    });
